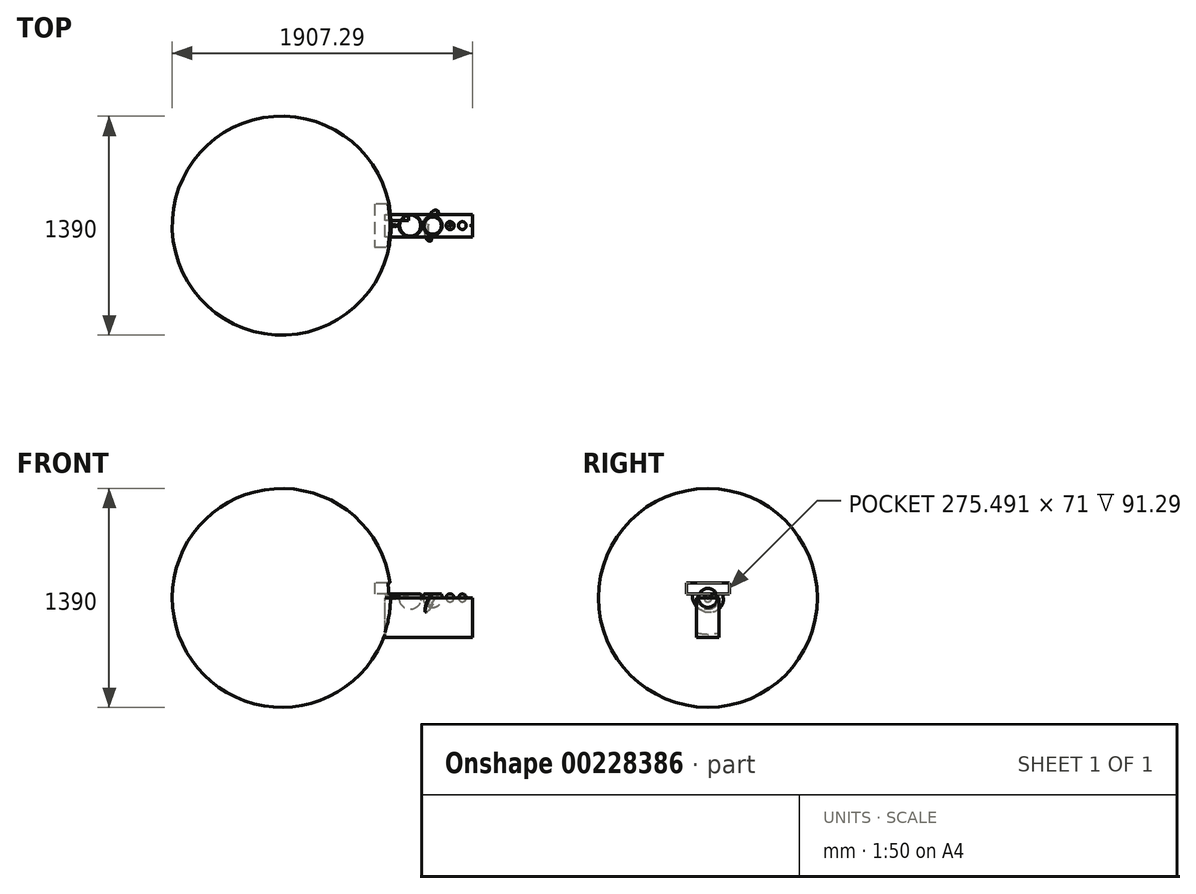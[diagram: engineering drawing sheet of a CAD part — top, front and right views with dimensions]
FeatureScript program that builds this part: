
annotation { "Feature Type Name" : "Feature", "Feature Type Description" : "" }
export const myFeature = defineFeature(function(context is Context, id is Id, definition is map)
    precondition{}
    {
        {
            assignVariable(context, id + "F0", {"name" : "SunD", "anyValue" : 1390});
        }
        {
            assignVariable(context, id + "F1", {"name" : "MercuryD", "anyValue" : 4.88});
        }
        {
            assignVariable(context, id + "F2", {"name" : "VenusD", "anyValue" : 12.1});
        }
        {
            assignVariable(context, id + "F3", {"name" : "EarthD", "anyValue" : 12.76});
        }
        {
            assignVariable(context, id + "F4", {"name" : "MarsD", "anyValue" : 6.8});
        }
        {
            assignVariable(context, id + "F5", {"name" : "JupiterD", "anyValue" : 143});
        }
        {
            assignVariable(context, id + "F6", {"name" : "SaturnD", "anyValue" : 120.5});
        }
        {
            assignVariable(context, id + "F7", {"name" : "UranusD", "anyValue" : 51.1});
        }
        {
            assignVariable(context, id + "F8", {"name" : "NeptuneD", "anyValue" : 49.5});
        }
        {
            assignVariable(context, id + "F9", {"name" : "PlutoD", "anyValue" : 2.35});
        }
        {
            var Q0;
            Q0=qCreatedBy(makeId("Top.planeOp"),FACE);
            var sketch = newSketch(context, id + "F10", { "sketchPlane" : qUnion([Q0])});
            skCircle(sketch, "E0", {"center": v(0, 0) * mm, "radius": 695 * mm});
            skCircle(sketch, "E1", {"center": v(0, 0) * mm, "radius": 2.44 * mm});
            skCircle(sketch, "E2", {"center": v(0, 0) * mm, "radius": 6.05 * mm});
            skCircle(sketch, "E3", {"center": v(0, 0) * mm, "radius": 6.38 * mm});
            skCircle(sketch, "E4", {"center": v(0, 0) * mm, "radius": 3.4 * mm});
            skCircle(sketch, "E5", {"center": v(0, 0) * mm, "radius": 71.5 * mm});
            skCircle(sketch, "E6", {"center": v(0, 0) * mm, "radius": 60.25 * mm});
            skCircle(sketch, "E7", {"center": v(0, 0) * mm, "radius": 25.55 * mm});
            skCircle(sketch, "E8", {"center": v(0, 0) * mm, "radius": 24.75 * mm});
            skCircle(sketch, "E9", {"center": v(0, 0) * mm, "radius": 1.18 * mm});
            skLineSegment(sketch, "E10", {"start": v(-694.4, -28.81) * mm, "end": v(0, 0) * mm});
            skLineSegment(sketch, "E11", {"start": v(0, 0) * mm, "end": v(694.4, 28.81) * mm});
            skCircle(sketch, "E12", {"center": v(0, 0) * mm, "radius": 100.25 * mm});
            skLineSegment(sketch, "E13", {"start": v(0, 0) * mm, "end": v(-4.16, 100.16) * mm, "construction": true});
            skSolve(sketch);
        }
        {
            var Q0;
            {var subQ0=sQuery(id+"F10.wireOp",EDGE,"E10");var subQ1=sQuery(id+"F10.wireOp",EDGE,"E1");var subQ2=makeQuery(id+"F10.imprint","INTERSECT",VERTEX,{"derivedFrom":[subQ1,subQ0]});Q0=makeQuery(id+"F10.imprint","IMPRINT",FACE,{"disambiguationData":[TD([[makeQuery(id+"F10.imprint","IMPRINT",EDGE,{"disambiguationData":[TD([[subQ2,1.0]])],"derivedFrom":subQ1}),1.0]])]});}
            var Q1;
            {var subQ0=sQuery(id+"F10.wireOp",EDGE,"E10");var subQ1=sQuery(id+"F10.wireOp",EDGE,"E9");var subQ2=makeQuery(id+"F10.imprint","INTERSECT",VERTEX,{"derivedFrom":[subQ1,subQ0]});Q1=makeQuery(id+"F10.imprint","IMPRINT",FACE,{"disambiguationData":[TD([[makeQuery(id+"F10.imprint","IMPRINT",EDGE,{"disambiguationData":[TD([[subQ2,1.0]])],"derivedFrom":subQ1}),1.0]])]});}
            var Q2;
            Q2=sQuery(id+"F10.wireOp",EDGE,"E10");
            revolve(context, id + "F11", {"entities" : qUnion([Q0, Q1]), "axis" : qUnion([Q2]), "revolveType" : RevolveType.FULL});
        }
        {
            var Q0;
            Q0=makeQuery(id+"F11.opRevolve","SWEPT_BODY",BODY,{"disambiguationData":[OSD([sQuery(id+"F10.wireOp",EDGE,"E1"),sQuery(id+"F10.wireOp",EDGE,"E10"),sQuery(id+"F10.wireOp",EDGE,"E11")])]});
            transform(context, id + "F12", {"entities" : qUnion([Q0]), "transformType" : TransformType.TRANSLATION_3D, "dx" : (getVariable(context, 'SunD') / 2 + getVariable(context, 'MercuryD') / 2 + 1) * mm, "dy" : 0 * mm, "dz" : 0 * mm, "makeCopy" : false});
        }
        {
            var Q0;
            {var subQ0=sQuery(id+"F10.wireOp",EDGE,"E10");var subQ1=sQuery(id+"F10.wireOp",EDGE,"E2");var subQ2=makeQuery(id+"F10.imprint","INTERSECT",VERTEX,{"derivedFrom":[subQ1,subQ0]});Q0=makeQuery(id+"F10.imprint","IMPRINT",FACE,{"disambiguationData":[TD([[makeQuery(id+"F10.imprint","IMPRINT",EDGE,{"disambiguationData":[TD([[subQ2,1.0]])],"derivedFrom":subQ1}),1.0]])]});}
            var Q1;
            {var subQ0=sQuery(id+"F10.wireOp",EDGE,"E10");var subQ1=sQuery(id+"F10.wireOp",EDGE,"E1");var subQ2=makeQuery(id+"F10.imprint","INTERSECT",VERTEX,{"derivedFrom":[subQ1,subQ0]});Q1=makeQuery(id+"F10.imprint","IMPRINT",FACE,{"disambiguationData":[TD([[makeQuery(id+"F10.imprint","IMPRINT",EDGE,{"disambiguationData":[TD([[subQ2,1.0]])],"derivedFrom":subQ1}),-1.0]])]});}
            var Q2;
            {var subQ0=sQuery(id+"F10.wireOp",EDGE,"E10");var subQ1=sQuery(id+"F10.wireOp",EDGE,"E1");var subQ2=makeQuery(id+"F10.imprint","INTERSECT",VERTEX,{"derivedFrom":[subQ1,subQ0]});Q2=makeQuery(id+"F10.imprint","IMPRINT",FACE,{"disambiguationData":[TD([[makeQuery(id+"F10.imprint","IMPRINT",EDGE,{"disambiguationData":[TD([[subQ2,1.0]])],"derivedFrom":subQ1}),1.0]])]});}
            var Q3;
            {var subQ0=sQuery(id+"F10.wireOp",EDGE,"E10");var subQ1=sQuery(id+"F10.wireOp",EDGE,"E9");var subQ2=makeQuery(id+"F10.imprint","INTERSECT",VERTEX,{"derivedFrom":[subQ1,subQ0]});Q3=makeQuery(id+"F10.imprint","IMPRINT",FACE,{"disambiguationData":[TD([[makeQuery(id+"F10.imprint","IMPRINT",EDGE,{"disambiguationData":[TD([[subQ2,1.0]])],"derivedFrom":subQ1}),1.0]])]});}
            var Q4;
            Q4=sQuery(id+"F10.wireOp",EDGE,"E11");
            revolve(context, id + "F13", {"entities" : qUnion([Q0, Q1, Q2, Q3]), "axis" : qUnion([Q4]), "revolveType" : RevolveType.FULL});
        }
        {
            var Q0;
            Q0=makeQuery(id+"F13.opRevolve","SWEPT_BODY",BODY,{"disambiguationData":[OSD([sQuery(id+"F10.wireOp",EDGE,"E2"),sQuery(id+"F10.wireOp",EDGE,"E10"),sQuery(id+"F10.wireOp",EDGE,"E11")])]});
            transform(context, id + "F14", {"entities" : qUnion([Q0]), "transformType" : TransformType.TRANSLATION_3D, "dx" : (getVariable(context, 'SunD') / 2 + getVariable(context, 'MercuryD') + getVariable(context, 'VenusD') / 2 + 0.72 / 0.39) * mm, "dy" : 0 * mm, "dz" : 0 * mm, "makeCopy" : false});
        }
        {
            var Q0;
            {var subQ0=sQuery(id+"F10.wireOp",EDGE,"E10");var subQ1=sQuery(id+"F10.wireOp",EDGE,"E2");var subQ2=makeQuery(id+"F10.imprint","INTERSECT",VERTEX,{"derivedFrom":[subQ1,subQ0]});Q0=makeQuery(id+"F10.imprint","IMPRINT",FACE,{"disambiguationData":[TD([[makeQuery(id+"F10.imprint","IMPRINT",EDGE,{"disambiguationData":[TD([[subQ2,1.0]])],"derivedFrom":subQ1}),-1.0]])]});}
            var Q1;
            {var subQ0=sQuery(id+"F10.wireOp",EDGE,"E10");var subQ1=sQuery(id+"F10.wireOp",EDGE,"E2");var subQ2=makeQuery(id+"F10.imprint","INTERSECT",VERTEX,{"derivedFrom":[subQ1,subQ0]});Q1=makeQuery(id+"F10.imprint","IMPRINT",FACE,{"disambiguationData":[TD([[makeQuery(id+"F10.imprint","IMPRINT",EDGE,{"disambiguationData":[TD([[subQ2,1.0]])],"derivedFrom":subQ1}),1.0]])]});}
            var Q2;
            {var subQ0=sQuery(id+"F10.wireOp",EDGE,"E10");var subQ1=sQuery(id+"F10.wireOp",EDGE,"E1");var subQ2=makeQuery(id+"F10.imprint","INTERSECT",VERTEX,{"derivedFrom":[subQ1,subQ0]});Q2=makeQuery(id+"F10.imprint","IMPRINT",FACE,{"disambiguationData":[TD([[makeQuery(id+"F10.imprint","IMPRINT",EDGE,{"disambiguationData":[TD([[subQ2,1.0]])],"derivedFrom":subQ1}),-1.0]])]});}
            var Q3;
            {var subQ0=sQuery(id+"F10.wireOp",EDGE,"E10");var subQ1=sQuery(id+"F10.wireOp",EDGE,"E1");var subQ2=makeQuery(id+"F10.imprint","INTERSECT",VERTEX,{"derivedFrom":[subQ1,subQ0]});Q3=makeQuery(id+"F10.imprint","IMPRINT",FACE,{"disambiguationData":[TD([[makeQuery(id+"F10.imprint","IMPRINT",EDGE,{"disambiguationData":[TD([[subQ2,1.0]])],"derivedFrom":subQ1}),1.0]])]});}
            var Q4;
            {var subQ0=sQuery(id+"F10.wireOp",EDGE,"E10");var subQ1=sQuery(id+"F10.wireOp",EDGE,"E9");var subQ2=makeQuery(id+"F10.imprint","INTERSECT",VERTEX,{"derivedFrom":[subQ1,subQ0]});Q4=makeQuery(id+"F10.imprint","IMPRINT",FACE,{"disambiguationData":[TD([[makeQuery(id+"F10.imprint","IMPRINT",EDGE,{"disambiguationData":[TD([[subQ2,1.0]])],"derivedFrom":subQ1}),1.0]])]});}
            var Q5;
            Q5=sQuery(id+"F10.wireOp",EDGE,"E10");
            revolve(context, id + "F15", {"entities" : qUnion([Q0, Q1, Q2, Q3, Q4]), "axis" : qUnion([Q5]), "revolveType" : RevolveType.FULL});
        }
        {
            var Q0;
            Q0=makeQuery(id+"F15.opRevolve","SWEPT_BODY",BODY,{"disambiguationData":[OSD([sQuery(id+"F10.wireOp",EDGE,"E3"),sQuery(id+"F10.wireOp",EDGE,"E10"),sQuery(id+"F10.wireOp",EDGE,"E11")])]});
            transform(context, id + "F16", {"entities" : qUnion([Q0]), "transformType" : TransformType.TRANSLATION_3D, "dx" : (getVariable(context, 'SunD') / 2 + getVariable(context, 'MercuryD') + getVariable(context, 'VenusD') + getVariable(context, 'EarthD') / 2 + 1 / 0.39) * mm, "dy" : 0 * mm, "dz" : 0 * mm, "makeCopy" : false});
        }
        {
            var Q0;
            {var subQ0=sQuery(id+"F10.wireOp",EDGE,"E10");var subQ1=sQuery(id+"F10.wireOp",EDGE,"E1");var subQ2=makeQuery(id+"F10.imprint","INTERSECT",VERTEX,{"derivedFrom":[subQ1,subQ0]});Q0=makeQuery(id+"F10.imprint","IMPRINT",FACE,{"disambiguationData":[TD([[makeQuery(id+"F10.imprint","IMPRINT",EDGE,{"disambiguationData":[TD([[subQ2,1.0]])],"derivedFrom":subQ1}),-1.0]])]});}
            var Q1;
            {var subQ0=sQuery(id+"F10.wireOp",EDGE,"E10");var subQ1=sQuery(id+"F10.wireOp",EDGE,"E1");var subQ2=makeQuery(id+"F10.imprint","INTERSECT",VERTEX,{"derivedFrom":[subQ1,subQ0]});Q1=makeQuery(id+"F10.imprint","IMPRINT",FACE,{"disambiguationData":[TD([[makeQuery(id+"F10.imprint","IMPRINT",EDGE,{"disambiguationData":[TD([[subQ2,1.0]])],"derivedFrom":subQ1}),1.0]])]});}
            var Q2;
            {var subQ0=sQuery(id+"F10.wireOp",EDGE,"E10");var subQ1=sQuery(id+"F10.wireOp",EDGE,"E9");var subQ2=makeQuery(id+"F10.imprint","INTERSECT",VERTEX,{"derivedFrom":[subQ1,subQ0]});Q2=makeQuery(id+"F10.imprint","IMPRINT",FACE,{"disambiguationData":[TD([[makeQuery(id+"F10.imprint","IMPRINT",EDGE,{"disambiguationData":[TD([[subQ2,1.0]])],"derivedFrom":subQ1}),1.0]])]});}
            var Q3;
            Q3=sQuery(id+"F10.wireOp",EDGE,"E11");
            revolve(context, id + "F17", {"entities" : qUnion([Q0, Q1, Q2]), "axis" : qUnion([Q3]), "revolveType" : RevolveType.FULL});
        }
        {
            var Q0;
            Q0=makeQuery(id+"F17.opRevolve","SWEPT_BODY",BODY,{"disambiguationData":[OSD([sQuery(id+"F10.wireOp",EDGE,"E4"),sQuery(id+"F10.wireOp",EDGE,"E10"),sQuery(id+"F10.wireOp",EDGE,"E11")])]});
            transform(context, id + "F18", {"entities" : qUnion([Q0]), "transformType" : TransformType.TRANSLATION_3D, "dx" : (getVariable(context, 'SunD') / 2 + getVariable(context, 'MercuryD') + getVariable(context, 'VenusD') + getVariable(context, 'EarthD') + getVariable(context, 'MarsD') / 2 + 1.52 / 0.39) * mm, "dy" : 0 * mm, "dz" : 0 * mm, "makeCopy" : false});
        }
        {
            var Q0;
            {var subQ0=sQuery(id+"F10.wireOp",EDGE,"E10");var subQ1=sQuery(id+"F10.wireOp",EDGE,"E5");var subQ2=makeQuery(id+"F10.imprint","INTERSECT",VERTEX,{"derivedFrom":[subQ1,subQ0]});Q0=makeQuery(id+"F10.imprint","IMPRINT",FACE,{"disambiguationData":[TD([[makeQuery(id+"F10.imprint","IMPRINT",EDGE,{"disambiguationData":[TD([[subQ2,1.0]])],"derivedFrom":subQ1}),1.0]])]});}
            var Q1;
            {var subQ0=sQuery(id+"F10.wireOp",EDGE,"E10");var subQ1=sQuery(id+"F10.wireOp",EDGE,"E6");var subQ2=makeQuery(id+"F10.imprint","INTERSECT",VERTEX,{"derivedFrom":[subQ1,subQ0]});Q1=makeQuery(id+"F10.imprint","IMPRINT",FACE,{"disambiguationData":[TD([[makeQuery(id+"F10.imprint","IMPRINT",EDGE,{"disambiguationData":[TD([[subQ2,1.0]])],"derivedFrom":subQ1}),1.0]])]});}
            var Q2;
            {var subQ0=sQuery(id+"F10.wireOp",EDGE,"E10");var subQ1=sQuery(id+"F10.wireOp",EDGE,"E3");var subQ2=makeQuery(id+"F10.imprint","INTERSECT",VERTEX,{"derivedFrom":[subQ1,subQ0]});Q2=makeQuery(id+"F10.imprint","IMPRINT",FACE,{"disambiguationData":[TD([[makeQuery(id+"F10.imprint","IMPRINT",EDGE,{"disambiguationData":[TD([[subQ2,1.0]])],"derivedFrom":subQ1}),-1.0]])]});}
            var Q3;
            {var subQ0=sQuery(id+"F10.wireOp",EDGE,"E10");var subQ1=sQuery(id+"F10.wireOp",EDGE,"E7");var subQ2=makeQuery(id+"F10.imprint","INTERSECT",VERTEX,{"derivedFrom":[subQ1,subQ0]});Q3=makeQuery(id+"F10.imprint","IMPRINT",FACE,{"disambiguationData":[TD([[makeQuery(id+"F10.imprint","IMPRINT",EDGE,{"disambiguationData":[TD([[subQ2,1.0]])],"derivedFrom":subQ1}),1.0]])]});}
            var Q4;
            {var subQ0=sQuery(id+"F10.wireOp",EDGE,"E10");var subQ1=sQuery(id+"F10.wireOp",EDGE,"E2");var subQ2=makeQuery(id+"F10.imprint","INTERSECT",VERTEX,{"derivedFrom":[subQ1,subQ0]});Q4=makeQuery(id+"F10.imprint","IMPRINT",FACE,{"disambiguationData":[TD([[makeQuery(id+"F10.imprint","IMPRINT",EDGE,{"disambiguationData":[TD([[subQ2,1.0]])],"derivedFrom":subQ1}),1.0]])]});}
            var Q5;
            {var subQ0=sQuery(id+"F10.wireOp",EDGE,"E10");var subQ1=sQuery(id+"F10.wireOp",EDGE,"E1");var subQ2=makeQuery(id+"F10.imprint","INTERSECT",VERTEX,{"derivedFrom":[subQ1,subQ0]});Q5=makeQuery(id+"F10.imprint","IMPRINT",FACE,{"disambiguationData":[TD([[makeQuery(id+"F10.imprint","IMPRINT",EDGE,{"disambiguationData":[TD([[subQ2,1.0]])],"derivedFrom":subQ1}),-1.0]])]});}
            var Q6;
            {var subQ0=sQuery(id+"F10.wireOp",EDGE,"E10");var subQ1=sQuery(id+"F10.wireOp",EDGE,"E1");var subQ2=makeQuery(id+"F10.imprint","INTERSECT",VERTEX,{"derivedFrom":[subQ1,subQ0]});Q6=makeQuery(id+"F10.imprint","IMPRINT",FACE,{"disambiguationData":[TD([[makeQuery(id+"F10.imprint","IMPRINT",EDGE,{"disambiguationData":[TD([[subQ2,1.0]])],"derivedFrom":subQ1}),1.0]])]});}
            var Q7;
            {var subQ0=sQuery(id+"F10.wireOp",EDGE,"E10");var subQ1=sQuery(id+"F10.wireOp",EDGE,"E9");var subQ2=makeQuery(id+"F10.imprint","INTERSECT",VERTEX,{"derivedFrom":[subQ1,subQ0]});Q7=makeQuery(id+"F10.imprint","IMPRINT",FACE,{"disambiguationData":[TD([[makeQuery(id+"F10.imprint","IMPRINT",EDGE,{"disambiguationData":[TD([[subQ2,1.0]])],"derivedFrom":subQ1}),1.0]])]});}
            var Q8;
            {var subQ0=sQuery(id+"F10.wireOp",EDGE,"E10");var subQ1=sQuery(id+"F10.wireOp",EDGE,"E2");var subQ2=makeQuery(id+"F10.imprint","INTERSECT",VERTEX,{"derivedFrom":[subQ1,subQ0]});Q8=makeQuery(id+"F10.imprint","IMPRINT",FACE,{"disambiguationData":[TD([[makeQuery(id+"F10.imprint","IMPRINT",EDGE,{"disambiguationData":[TD([[subQ2,1.0]])],"derivedFrom":subQ1}),-1.0]])]});}
            var Q9;
            Q9=sQuery(id+"F10.wireOp",EDGE,"E11");
            revolve(context, id + "F19", {"entities" : qUnion([Q0, Q1, Q2, Q3, Q4, Q5, Q6, Q7, Q8]), "axis" : qUnion([Q9]), "revolveType" : RevolveType.FULL});
        }
        {
            var Q0;
            Q0=makeQuery(id+"F19.opRevolve","SWEPT_BODY",BODY,{"disambiguationData":[OSD([sQuery(id+"F10.wireOp",EDGE,"E5"),sQuery(id+"F10.wireOp",EDGE,"E10"),sQuery(id+"F10.wireOp",EDGE,"E11")])]});
            transform(context, id + "F20", {"entities" : qUnion([Q0]), "transformType" : TransformType.TRANSLATION_3D, "dx" : (getVariable(context, 'SunD') / 2 + getVariable(context, 'MercuryD') + getVariable(context, 'VenusD') + getVariable(context, 'EarthD') + getVariable(context, 'MarsD') + getVariable(context, 'JupiterD') / 2 + 5.3 / 0.39) * mm, "dy" : 0 * mm, "dz" : 0 * mm, "makeCopy" : false});
        }
        {
            var Q0;
            {var subQ0=sQuery(id+"F10.wireOp",EDGE,"E10");var subQ1=sQuery(id+"F10.wireOp",EDGE,"E6");var subQ2=makeQuery(id+"F10.imprint","INTERSECT",VERTEX,{"derivedFrom":[subQ1,subQ0]});Q0=makeQuery(id+"F10.imprint","IMPRINT",FACE,{"disambiguationData":[TD([[makeQuery(id+"F10.imprint","IMPRINT",EDGE,{"disambiguationData":[TD([[subQ2,1.0]])],"derivedFrom":subQ1}),1.0]])]});}
            var Q1;
            {var subQ0=sQuery(id+"F10.wireOp",EDGE,"E10");var subQ1=sQuery(id+"F10.wireOp",EDGE,"E7");var subQ2=makeQuery(id+"F10.imprint","INTERSECT",VERTEX,{"derivedFrom":[subQ1,subQ0]});Q1=makeQuery(id+"F10.imprint","IMPRINT",FACE,{"disambiguationData":[TD([[makeQuery(id+"F10.imprint","IMPRINT",EDGE,{"disambiguationData":[TD([[subQ2,1.0]])],"derivedFrom":subQ1}),1.0]])]});}
            var Q2;
            {var subQ0=sQuery(id+"F10.wireOp",EDGE,"E10");var subQ1=sQuery(id+"F10.wireOp",EDGE,"E3");var subQ2=makeQuery(id+"F10.imprint","INTERSECT",VERTEX,{"derivedFrom":[subQ1,subQ0]});Q2=makeQuery(id+"F10.imprint","IMPRINT",FACE,{"disambiguationData":[TD([[makeQuery(id+"F10.imprint","IMPRINT",EDGE,{"disambiguationData":[TD([[subQ2,1.0]])],"derivedFrom":subQ1}),-1.0]])]});}
            var Q3;
            {var subQ0=sQuery(id+"F10.wireOp",EDGE,"E10");var subQ1=sQuery(id+"F10.wireOp",EDGE,"E2");var subQ2=makeQuery(id+"F10.imprint","INTERSECT",VERTEX,{"derivedFrom":[subQ1,subQ0]});Q3=makeQuery(id+"F10.imprint","IMPRINT",FACE,{"disambiguationData":[TD([[makeQuery(id+"F10.imprint","IMPRINT",EDGE,{"disambiguationData":[TD([[subQ2,1.0]])],"derivedFrom":subQ1}),1.0]])]});}
            var Q4;
            {var subQ0=sQuery(id+"F10.wireOp",EDGE,"E10");var subQ1=sQuery(id+"F10.wireOp",EDGE,"E1");var subQ2=makeQuery(id+"F10.imprint","INTERSECT",VERTEX,{"derivedFrom":[subQ1,subQ0]});Q4=makeQuery(id+"F10.imprint","IMPRINT",FACE,{"disambiguationData":[TD([[makeQuery(id+"F10.imprint","IMPRINT",EDGE,{"disambiguationData":[TD([[subQ2,1.0]])],"derivedFrom":subQ1}),-1.0]])]});}
            var Q5;
            {var subQ0=sQuery(id+"F10.wireOp",EDGE,"E10");var subQ1=sQuery(id+"F10.wireOp",EDGE,"E1");var subQ2=makeQuery(id+"F10.imprint","INTERSECT",VERTEX,{"derivedFrom":[subQ1,subQ0]});Q5=makeQuery(id+"F10.imprint","IMPRINT",FACE,{"disambiguationData":[TD([[makeQuery(id+"F10.imprint","IMPRINT",EDGE,{"disambiguationData":[TD([[subQ2,1.0]])],"derivedFrom":subQ1}),1.0]])]});}
            var Q6;
            {var subQ0=sQuery(id+"F10.wireOp",EDGE,"E10");var subQ1=sQuery(id+"F10.wireOp",EDGE,"E9");var subQ2=makeQuery(id+"F10.imprint","INTERSECT",VERTEX,{"derivedFrom":[subQ1,subQ0]});Q6=makeQuery(id+"F10.imprint","IMPRINT",FACE,{"disambiguationData":[TD([[makeQuery(id+"F10.imprint","IMPRINT",EDGE,{"disambiguationData":[TD([[subQ2,1.0]])],"derivedFrom":subQ1}),1.0]])]});}
            var Q7;
            {var subQ0=sQuery(id+"F10.wireOp",EDGE,"E10");var subQ1=sQuery(id+"F10.wireOp",EDGE,"E2");var subQ2=makeQuery(id+"F10.imprint","INTERSECT",VERTEX,{"derivedFrom":[subQ1,subQ0]});Q7=makeQuery(id+"F10.imprint","IMPRINT",FACE,{"disambiguationData":[TD([[makeQuery(id+"F10.imprint","IMPRINT",EDGE,{"disambiguationData":[TD([[subQ2,1.0]])],"derivedFrom":subQ1}),-1.0]])]});}
            var Q8;
            Q8=sQuery(id+"F10.wireOp",EDGE,"E10");
            revolve(context, id + "F21", {"entities" : qUnion([Q0, Q1, Q2, Q3, Q4, Q5, Q6, Q7]), "axis" : qUnion([Q8]), "revolveType" : RevolveType.FULL});
        }
        {
            var Q0;
            {var subQ0=sQuery(id+"F10.wireOp",EDGE,"E10");var subQ1=sQuery(id+"F10.wireOp",EDGE,"E5");var subQ2=makeQuery(id+"F10.imprint","INTERSECT",VERTEX,{"derivedFrom":[subQ1,subQ0]});Q0=makeQuery(id+"F10.imprint","IMPRINT",FACE,{"disambiguationData":[TD([[makeQuery(id+"F10.imprint","IMPRINT",EDGE,{"disambiguationData":[TD([[subQ2,1.0]])],"derivedFrom":subQ1}),-1.0]])]});}
            var Q1;
            {var subQ0=sQuery(id+"F10.wireOp",EDGE,"E10");var subQ1=sQuery(id+"F10.wireOp",EDGE,"E5");var subQ2=makeQuery(id+"F10.imprint","INTERSECT",VERTEX,{"derivedFrom":[subQ1,subQ0]});Q1=makeQuery(id+"F10.imprint","IMPRINT",FACE,{"disambiguationData":[TD([[makeQuery(id+"F10.imprint","IMPRINT",EDGE,{"disambiguationData":[TD([[subQ2,1.0]])],"derivedFrom":subQ1}),1.0]])]});}
            var Q2;
            {var subQ0=sQuery(id+"F10.wireOp",EDGE,"E10");var subQ1=sQuery(id+"F10.wireOp",EDGE,"E5");var subQ2=makeQuery(id+"F10.imprint","INTERSECT",VERTEX,{"derivedFrom":[subQ1,subQ0]});Q2=makeQuery(id+"F10.imprint","IMPRINT",FACE,{"disambiguationData":[TD([[makeQuery(id+"F10.imprint","IMPRINT",EDGE,{"disambiguationData":[TD([[subQ2,-1.0]])],"derivedFrom":subQ1}),1.0]])]});}
            var Q3;
            {var subQ0=sQuery(id+"F10.wireOp",EDGE,"E10");var subQ1=sQuery(id+"F10.wireOp",EDGE,"E5");var subQ2=makeQuery(id+"F10.imprint","INTERSECT",VERTEX,{"derivedFrom":[subQ1,subQ0]});Q3=makeQuery(id+"F10.imprint","IMPRINT",FACE,{"disambiguationData":[TD([[makeQuery(id+"F10.imprint","IMPRINT",EDGE,{"disambiguationData":[TD([[subQ2,-1.0]])],"derivedFrom":subQ1}),-1.0]])]});}
            var Q4;
            {var subQ0=sQuery(id+"F10.wireOp",EDGE,"E10");var subQ1=sQuery(id+"F10.wireOp",EDGE,"E6");var subQ2=makeQuery(id+"F10.imprint","INTERSECT",VERTEX,{"derivedFrom":[subQ1,subQ0]});Q4=makeQuery(id+"F10.imprint","IMPRINT",FACE,{"disambiguationData":[TD([[makeQuery(id+"F10.imprint","IMPRINT",EDGE,{"disambiguationData":[TD([[subQ2,-1.0]])],"derivedFrom":subQ1}),1.0]])]});}
            var Q5;
            {var subQ0=sQuery(id+"F10.wireOp",EDGE,"E10");var subQ1=sQuery(id+"F10.wireOp",EDGE,"E6");var subQ2=makeQuery(id+"F10.imprint","INTERSECT",VERTEX,{"derivedFrom":[subQ1,subQ0]});Q5=makeQuery(id+"F10.imprint","IMPRINT",FACE,{"disambiguationData":[TD([[makeQuery(id+"F10.imprint","IMPRINT",EDGE,{"disambiguationData":[TD([[subQ2,1.0]])],"derivedFrom":subQ1}),1.0]])]});}
            extrude(context, id + "F22", {"entities" : qUnion([Q0, Q1, Q2, Q3, Q4, Q5]), "operationType" : NewBodyOperationType.ADD, "depth" : 3 * mm, "symmetric" : true});
        }
        {
            var Q0;
            Q0=makeQuery(id+"F21.opRevolve","SWEPT_BODY",BODY,{"disambiguationData":[OSD([sQuery(id+"F10.wireOp",EDGE,"E6"),sQuery(id+"F10.wireOp",EDGE,"E10"),sQuery(id+"F10.wireOp",EDGE,"E11")])]});
            var Q1;
            Q1=sQuery(id+"F10.wireOp",EDGE,"E13");
            transform(context, id + "F23", {"entities" : qUnion([Q0]), "transformType" : TransformType.ROTATION, "transformAxis" : qUnion([Q1]), "angle" : 120 * degree, "makeCopy" : false});
        }
        {
            var Q0;
            Q0=makeQuery(id+"F21.opRevolve","SWEPT_BODY",BODY,{"disambiguationData":[OSD([sQuery(id+"F10.wireOp",EDGE,"E6"),sQuery(id+"F10.wireOp",EDGE,"E10"),sQuery(id+"F10.wireOp",EDGE,"E11")])]});
            var Q1;
            Q1=sQuery(id+"F10.wireOp",EDGE,"E10");
            transform(context, id + "F24", {"entities" : qUnion([Q0]), "transformType" : TransformType.ROTATION, "transformAxis" : qUnion([Q1]), "angle" : 30 * degree, "oppositeDirection" : true, "makeCopy" : false});
        }
        {
            var Q0;
            Q0=makeQuery(id+"F21.opRevolve","SWEPT_BODY",BODY,{"disambiguationData":[OSD([sQuery(id+"F10.wireOp",EDGE,"E6"),sQuery(id+"F10.wireOp",EDGE,"E10"),sQuery(id+"F10.wireOp",EDGE,"E11")])]});
            transform(context, id + "F25", {"entities" : qUnion([Q0]), "transformType" : TransformType.TRANSLATION_3D, "dx" : (getVariable(context, 'SunD') / 2 + getVariable(context, 'MercuryD') + getVariable(context, 'VenusD') + getVariable(context, 'EarthD') + getVariable(context, 'MarsD') + getVariable(context, 'JupiterD') + getVariable(context, 'SaturnD') / 2 + 9.52 / 0.39) * mm, "dy" : 0 * mm, "dz" : 0 * mm, "makeCopy" : false});
        }
        {
            var Q0;
            {var subQ0=sQuery(id+"F10.wireOp",EDGE,"E10");var subQ1=sQuery(id+"F10.wireOp",EDGE,"E3");var subQ2=makeQuery(id+"F10.imprint","INTERSECT",VERTEX,{"derivedFrom":[subQ1,subQ0]});Q0=makeQuery(id+"F10.imprint","IMPRINT",FACE,{"disambiguationData":[TD([[makeQuery(id+"F10.imprint","IMPRINT",EDGE,{"disambiguationData":[TD([[subQ2,1.0]])],"derivedFrom":subQ1}),-1.0]])]});}
            var Q1;
            {var subQ0=sQuery(id+"F10.wireOp",EDGE,"E10");var subQ1=sQuery(id+"F10.wireOp",EDGE,"E2");var subQ2=makeQuery(id+"F10.imprint","INTERSECT",VERTEX,{"derivedFrom":[subQ1,subQ0]});Q1=makeQuery(id+"F10.imprint","IMPRINT",FACE,{"disambiguationData":[TD([[makeQuery(id+"F10.imprint","IMPRINT",EDGE,{"disambiguationData":[TD([[subQ2,1.0]])],"derivedFrom":subQ1}),1.0]])]});}
            var Q2;
            {var subQ0=sQuery(id+"F10.wireOp",EDGE,"E10");var subQ1=sQuery(id+"F10.wireOp",EDGE,"E1");var subQ2=makeQuery(id+"F10.imprint","INTERSECT",VERTEX,{"derivedFrom":[subQ1,subQ0]});Q2=makeQuery(id+"F10.imprint","IMPRINT",FACE,{"disambiguationData":[TD([[makeQuery(id+"F10.imprint","IMPRINT",EDGE,{"disambiguationData":[TD([[subQ2,1.0]])],"derivedFrom":subQ1}),-1.0]])]});}
            var Q3;
            {var subQ0=sQuery(id+"F10.wireOp",EDGE,"E10");var subQ1=sQuery(id+"F10.wireOp",EDGE,"E1");var subQ2=makeQuery(id+"F10.imprint","INTERSECT",VERTEX,{"derivedFrom":[subQ1,subQ0]});Q3=makeQuery(id+"F10.imprint","IMPRINT",FACE,{"disambiguationData":[TD([[makeQuery(id+"F10.imprint","IMPRINT",EDGE,{"disambiguationData":[TD([[subQ2,1.0]])],"derivedFrom":subQ1}),1.0]])]});}
            var Q4;
            {var subQ0=sQuery(id+"F10.wireOp",EDGE,"E10");var subQ1=sQuery(id+"F10.wireOp",EDGE,"E9");var subQ2=makeQuery(id+"F10.imprint","INTERSECT",VERTEX,{"derivedFrom":[subQ1,subQ0]});Q4=makeQuery(id+"F10.imprint","IMPRINT",FACE,{"disambiguationData":[TD([[makeQuery(id+"F10.imprint","IMPRINT",EDGE,{"disambiguationData":[TD([[subQ2,1.0]])],"derivedFrom":subQ1}),1.0]])]});}
            var Q5;
            {var subQ0=sQuery(id+"F10.wireOp",EDGE,"E10");var subQ1=sQuery(id+"F10.wireOp",EDGE,"E2");var subQ2=makeQuery(id+"F10.imprint","INTERSECT",VERTEX,{"derivedFrom":[subQ1,subQ0]});Q5=makeQuery(id+"F10.imprint","IMPRINT",FACE,{"disambiguationData":[TD([[makeQuery(id+"F10.imprint","IMPRINT",EDGE,{"disambiguationData":[TD([[subQ2,1.0]])],"derivedFrom":subQ1}),-1.0]])]});}
            var Q6;
            {var subQ0=sQuery(id+"F10.wireOp",EDGE,"E10");var subQ1=sQuery(id+"F10.wireOp",EDGE,"E7");var subQ2=makeQuery(id+"F10.imprint","INTERSECT",VERTEX,{"derivedFrom":[subQ1,subQ0]});Q6=makeQuery(id+"F10.imprint","IMPRINT",FACE,{"disambiguationData":[TD([[makeQuery(id+"F10.imprint","IMPRINT",EDGE,{"disambiguationData":[TD([[subQ2,1.0]])],"derivedFrom":subQ1}),1.0]])]});}
            var Q7;
            Q7=sQuery(id+"F10.wireOp",EDGE,"E10");
            revolve(context, id + "F26", {"entities" : qUnion([Q0, Q1, Q2, Q3, Q4, Q5, Q6]), "axis" : qUnion([Q7]), "revolveType" : RevolveType.FULL});
        }
        {
            var Q0;
            Q0=makeQuery(id+"F26.opRevolve","SWEPT_BODY",BODY,{"disambiguationData":[OSD([sQuery(id+"F10.wireOp",EDGE,"E7"),sQuery(id+"F10.wireOp",EDGE,"E10"),sQuery(id+"F10.wireOp",EDGE,"E11")])]});
            transform(context, id + "F27", {"entities" : qUnion([Q0]), "transformType" : TransformType.TRANSLATION_3D, "dx" : (getVariable(context, 'SunD') / 2 + getVariable(context, 'MercuryD') + getVariable(context, 'VenusD') + getVariable(context, 'EarthD') + getVariable(context, 'MarsD') + getVariable(context, 'JupiterD') + getVariable(context, 'SaturnD') + getVariable(context, 'UranusD') / 2 + 19.2 / 0.39) * mm, "dy" : 0 * mm, "dz" : 0 * mm, "makeCopy" : false});
        }
        {
            var Q0;
            {var subQ0=sQuery(id+"F10.wireOp",EDGE,"E10");var subQ1=sQuery(id+"F10.wireOp",EDGE,"E9");var subQ2=makeQuery(id+"F10.imprint","INTERSECT",VERTEX,{"derivedFrom":[subQ1,subQ0]});Q0=makeQuery(id+"F10.imprint","IMPRINT",FACE,{"disambiguationData":[TD([[makeQuery(id+"F10.imprint","IMPRINT",EDGE,{"disambiguationData":[TD([[subQ2,1.0]])],"derivedFrom":subQ1}),1.0]])]});}
            var Q1;
            {var subQ0=sQuery(id+"F10.wireOp",EDGE,"E10");var subQ1=sQuery(id+"F10.wireOp",EDGE,"E1");var subQ2=makeQuery(id+"F10.imprint","INTERSECT",VERTEX,{"derivedFrom":[subQ1,subQ0]});Q1=makeQuery(id+"F10.imprint","IMPRINT",FACE,{"disambiguationData":[TD([[makeQuery(id+"F10.imprint","IMPRINT",EDGE,{"disambiguationData":[TD([[subQ2,1.0]])],"derivedFrom":subQ1}),1.0]])]});}
            var Q2;
            {var subQ0=sQuery(id+"F10.wireOp",EDGE,"E10");var subQ1=sQuery(id+"F10.wireOp",EDGE,"E1");var subQ2=makeQuery(id+"F10.imprint","INTERSECT",VERTEX,{"derivedFrom":[subQ1,subQ0]});Q2=makeQuery(id+"F10.imprint","IMPRINT",FACE,{"disambiguationData":[TD([[makeQuery(id+"F10.imprint","IMPRINT",EDGE,{"disambiguationData":[TD([[subQ2,1.0]])],"derivedFrom":subQ1}),-1.0]])]});}
            var Q3;
            {var subQ0=sQuery(id+"F10.wireOp",EDGE,"E10");var subQ1=sQuery(id+"F10.wireOp",EDGE,"E2");var subQ2=makeQuery(id+"F10.imprint","INTERSECT",VERTEX,{"derivedFrom":[subQ1,subQ0]});Q3=makeQuery(id+"F10.imprint","IMPRINT",FACE,{"disambiguationData":[TD([[makeQuery(id+"F10.imprint","IMPRINT",EDGE,{"disambiguationData":[TD([[subQ2,1.0]])],"derivedFrom":subQ1}),1.0]])]});}
            var Q4;
            {var subQ0=sQuery(id+"F10.wireOp",EDGE,"E10");var subQ1=sQuery(id+"F10.wireOp",EDGE,"E2");var subQ2=makeQuery(id+"F10.imprint","INTERSECT",VERTEX,{"derivedFrom":[subQ1,subQ0]});Q4=makeQuery(id+"F10.imprint","IMPRINT",FACE,{"disambiguationData":[TD([[makeQuery(id+"F10.imprint","IMPRINT",EDGE,{"disambiguationData":[TD([[subQ2,1.0]])],"derivedFrom":subQ1}),-1.0]])]});}
            var Q5;
            {var subQ0=sQuery(id+"F10.wireOp",EDGE,"E10");var subQ1=sQuery(id+"F10.wireOp",EDGE,"E3");var subQ2=makeQuery(id+"F10.imprint","INTERSECT",VERTEX,{"derivedFrom":[subQ1,subQ0]});Q5=makeQuery(id+"F10.imprint","IMPRINT",FACE,{"disambiguationData":[TD([[makeQuery(id+"F10.imprint","IMPRINT",EDGE,{"disambiguationData":[TD([[subQ2,1.0]])],"derivedFrom":subQ1}),-1.0]])]});}
            var Q6;
            Q6=sQuery(id+"F10.wireOp",EDGE,"E10");
            revolve(context, id + "F28", {"entities" : qUnion([Q0, Q1, Q2, Q3, Q4, Q5]), "axis" : qUnion([Q6]), "revolveType" : RevolveType.FULL});
        }
        {
            var Q0;
            Q0=makeQuery(id+"F28.opRevolve","SWEPT_BODY",BODY,{"disambiguationData":[OSD([sQuery(id+"F10.wireOp",EDGE,"E8"),sQuery(id+"F10.wireOp",EDGE,"E10"),sQuery(id+"F10.wireOp",EDGE,"E11")])]});
            transform(context, id + "F29", {"entities" : qUnion([Q0]), "transformType" : TransformType.TRANSLATION_3D, "dx" : (getVariable(context, 'SunD') / 2 + getVariable(context, 'MercuryD') + getVariable(context, 'VenusD') + getVariable(context, 'EarthD') + getVariable(context, 'MarsD') + getVariable(context, 'JupiterD') + getVariable(context, 'SaturnD') + getVariable(context, 'UranusD') + getVariable(context, 'NeptuneD') / 2 + 30 / 0.39) * mm, "dy" : 0 * mm, "dz" : 0 * mm, "makeCopy" : false});
        }
        {
            var Q0;
            {var subQ0=sQuery(id+"F10.wireOp",EDGE,"E10");var subQ1=sQuery(id+"F10.wireOp",EDGE,"E9");var subQ2=makeQuery(id+"F10.imprint","INTERSECT",VERTEX,{"derivedFrom":[subQ1,subQ0]});Q0=makeQuery(id+"F10.imprint","IMPRINT",FACE,{"disambiguationData":[TD([[makeQuery(id+"F10.imprint","IMPRINT",EDGE,{"disambiguationData":[TD([[subQ2,1.0]])],"derivedFrom":subQ1}),1.0]])]});}
            var Q1;
            Q1=sQuery(id+"F10.wireOp",EDGE,"E10");
            revolve(context, id + "F30", {"entities" : qUnion([Q0]), "axis" : qUnion([Q1]), "revolveType" : RevolveType.FULL});
        }
        {
            var Q0;
            Q0=makeQuery(id+"F30.opRevolve","SWEPT_BODY",BODY,{"disambiguationData":[OSD([sQuery(id+"F10.wireOp",EDGE,"E9"),sQuery(id+"F10.wireOp",EDGE,"E10"),sQuery(id+"F10.wireOp",EDGE,"E11")])]});
            transform(context, id + "F31", {"entities" : qUnion([Q0]), "transformType" : TransformType.TRANSLATION_3D, "dx" : (getVariable(context, 'SunD') / 2 + getVariable(context, 'MercuryD') + getVariable(context, 'VenusD') + getVariable(context, 'EarthD') + getVariable(context, 'MarsD') + getVariable(context, 'JupiterD') + getVariable(context, 'SaturnD') + getVariable(context, 'UranusD') + getVariable(context, 'NeptuneD') + getVariable(context, 'PlutoD') / 2 + 39.5 / 0.39) * mm, "dy" : 0 * mm, "dz" : 0 * mm, "makeCopy" : false});
        }
        {
            var Q0;
            {var subQ0=sQuery(id+"F10.wireOp",EDGE,"E10");var subQ1=sQuery(id+"F10.wireOp",EDGE,"E0");var subQ2=makeQuery(id+"F10.imprint","INTERSECT",VERTEX,{"derivedFrom":[subQ1,subQ0]});Q0=makeQuery(id+"F10.imprint","IMPRINT",FACE,{"disambiguationData":[TD([[makeQuery(id+"F10.imprint","IMPRINT",EDGE,{"disambiguationData":[TD([[subQ2,1.0]])],"derivedFrom":subQ1}),1.0]])]});}
            var Q1;
            {var subQ0=sQuery(id+"F10.wireOp",EDGE,"E10");var subQ1=sQuery(id+"F10.wireOp",EDGE,"E5");var subQ2=makeQuery(id+"F10.imprint","INTERSECT",VERTEX,{"derivedFrom":[subQ1,subQ0]});Q1=makeQuery(id+"F10.imprint","IMPRINT",FACE,{"disambiguationData":[TD([[makeQuery(id+"F10.imprint","IMPRINT",EDGE,{"disambiguationData":[TD([[subQ2,1.0]])],"derivedFrom":subQ1}),-1.0]])]});}
            var Q2;
            {var subQ0=sQuery(id+"F10.wireOp",EDGE,"E10");var subQ1=sQuery(id+"F10.wireOp",EDGE,"E5");var subQ2=makeQuery(id+"F10.imprint","INTERSECT",VERTEX,{"derivedFrom":[subQ1,subQ0]});Q2=makeQuery(id+"F10.imprint","IMPRINT",FACE,{"disambiguationData":[TD([[makeQuery(id+"F10.imprint","IMPRINT",EDGE,{"disambiguationData":[TD([[subQ2,1.0]])],"derivedFrom":subQ1}),1.0]])]});}
            var Q3;
            {var subQ0=sQuery(id+"F10.wireOp",EDGE,"E10");var subQ1=sQuery(id+"F10.wireOp",EDGE,"E6");var subQ2=makeQuery(id+"F10.imprint","INTERSECT",VERTEX,{"derivedFrom":[subQ1,subQ0]});Q3=makeQuery(id+"F10.imprint","IMPRINT",FACE,{"disambiguationData":[TD([[makeQuery(id+"F10.imprint","IMPRINT",EDGE,{"disambiguationData":[TD([[subQ2,1.0]])],"derivedFrom":subQ1}),1.0]])]});}
            var Q4;
            {var subQ0=sQuery(id+"F10.wireOp",EDGE,"E10");var subQ1=sQuery(id+"F10.wireOp",EDGE,"E7");var subQ2=makeQuery(id+"F10.imprint","INTERSECT",VERTEX,{"derivedFrom":[subQ1,subQ0]});Q4=makeQuery(id+"F10.imprint","IMPRINT",FACE,{"disambiguationData":[TD([[makeQuery(id+"F10.imprint","IMPRINT",EDGE,{"disambiguationData":[TD([[subQ2,1.0]])],"derivedFrom":subQ1}),1.0]])]});}
            var Q5;
            {var subQ0=sQuery(id+"F10.wireOp",EDGE,"E10");var subQ1=sQuery(id+"F10.wireOp",EDGE,"E3");var subQ2=makeQuery(id+"F10.imprint","INTERSECT",VERTEX,{"derivedFrom":[subQ1,subQ0]});Q5=makeQuery(id+"F10.imprint","IMPRINT",FACE,{"disambiguationData":[TD([[makeQuery(id+"F10.imprint","IMPRINT",EDGE,{"disambiguationData":[TD([[subQ2,1.0]])],"derivedFrom":subQ1}),-1.0]])]});}
            var Q6;
            {var subQ0=sQuery(id+"F10.wireOp",EDGE,"E10");var subQ1=sQuery(id+"F10.wireOp",EDGE,"E2");var subQ2=makeQuery(id+"F10.imprint","INTERSECT",VERTEX,{"derivedFrom":[subQ1,subQ0]});Q6=makeQuery(id+"F10.imprint","IMPRINT",FACE,{"disambiguationData":[TD([[makeQuery(id+"F10.imprint","IMPRINT",EDGE,{"disambiguationData":[TD([[subQ2,1.0]])],"derivedFrom":subQ1}),-1.0]])]});}
            var Q7;
            {var subQ0=sQuery(id+"F10.wireOp",EDGE,"E10");var subQ1=sQuery(id+"F10.wireOp",EDGE,"E2");var subQ2=makeQuery(id+"F10.imprint","INTERSECT",VERTEX,{"derivedFrom":[subQ1,subQ0]});Q7=makeQuery(id+"F10.imprint","IMPRINT",FACE,{"disambiguationData":[TD([[makeQuery(id+"F10.imprint","IMPRINT",EDGE,{"disambiguationData":[TD([[subQ2,1.0]])],"derivedFrom":subQ1}),1.0]])]});}
            var Q8;
            {var subQ0=sQuery(id+"F10.wireOp",EDGE,"E10");var subQ1=sQuery(id+"F10.wireOp",EDGE,"E1");var subQ2=makeQuery(id+"F10.imprint","INTERSECT",VERTEX,{"derivedFrom":[subQ1,subQ0]});Q8=makeQuery(id+"F10.imprint","IMPRINT",FACE,{"disambiguationData":[TD([[makeQuery(id+"F10.imprint","IMPRINT",EDGE,{"disambiguationData":[TD([[subQ2,1.0]])],"derivedFrom":subQ1}),-1.0]])]});}
            var Q9;
            {var subQ0=sQuery(id+"F10.wireOp",EDGE,"E10");var subQ1=sQuery(id+"F10.wireOp",EDGE,"E1");var subQ2=makeQuery(id+"F10.imprint","INTERSECT",VERTEX,{"derivedFrom":[subQ1,subQ0]});Q9=makeQuery(id+"F10.imprint","IMPRINT",FACE,{"disambiguationData":[TD([[makeQuery(id+"F10.imprint","IMPRINT",EDGE,{"disambiguationData":[TD([[subQ2,1.0]])],"derivedFrom":subQ1}),1.0]])]});}
            var Q10;
            {var subQ0=sQuery(id+"F10.wireOp",EDGE,"E10");var subQ1=sQuery(id+"F10.wireOp",EDGE,"E9");var subQ2=makeQuery(id+"F10.imprint","INTERSECT",VERTEX,{"derivedFrom":[subQ1,subQ0]});Q10=makeQuery(id+"F10.imprint","IMPRINT",FACE,{"disambiguationData":[TD([[makeQuery(id+"F10.imprint","IMPRINT",EDGE,{"disambiguationData":[TD([[subQ2,1.0]])],"derivedFrom":subQ1}),1.0]])]});}
            var Q11;
            Q11=sQuery(id+"F10.wireOp",EDGE,"E10");
            revolve(context, id + "F32", {"entities" : qUnion([Q0, Q1, Q2, Q3, Q4, Q5, Q6, Q7, Q8, Q9, Q10]), "axis" : qUnion([Q11]), "revolveType" : RevolveType.FULL});
        }
        {
            var Q0;
            Q0=qCreatedBy(makeId("Top.planeOp"),FACE);
            var sketch = newSketch(context, id + "F33", { "sketchPlane" : qUnion([Q0])});
            skCircle(sketch, "E14", {"center": v(816.62, 0) * mm, "radius": 71.5 * mm, "construction": true});
            skLineSegment(sketch, "E15", {"start": v(816.62, 71.5) * mm, "end": v(1212.3, 71.5) * mm});
            skLineSegment(sketch, "E16", {"start": v(816.62, -71.5) * mm, "end": v(1212.3, -71.5) * mm});
            skLineSegment(sketch, "E17", {"start": v(816.62, -71.5) * mm, "end": v(655.7, -71.5) * mm});
            skLineSegment(sketch, "E18", {"start": v(655.7, -71.5) * mm, "end": v(655.7, 71.5) * mm});
            skLineSegment(sketch, "E19", {"start": v(655.7, 71.5) * mm, "end": v(816.62, 71.5) * mm});
            skLineSegment(sketch, "E20", {"start": v(1212.3, -71.5) * mm, "end": v(1212.3, 71.5) * mm});
            skSolve(sketch);
        }
        {
            var Q0;
            Q0=makeQuery(id+"F33.imprint","IMPRINT",FACE,{"disambiguationData":[TD([[makeQuery(id+"F33.imprint","IMPRINT",EDGE,{"derivedFrom":sQuery(id+"F33.wireOp",EDGE,"E15")}),-1.0]])]});
            var Q1;
            Q1=sQuery(id+"F33.wireOp",EDGE,"E14");
            var Q2;
            Q2=makeQuery(id+"F19.opRevolve","SWEPT_BODY",BODY,{"disambiguationData":[OSD([sQuery(id+"F10.wireOp",EDGE,"E5"),sQuery(id+"F10.wireOp",EDGE,"E10"),sQuery(id+"F10.wireOp",EDGE,"E11")])]});
            extrude(context, id + "F34", {"entities" : qUnion([Q0]), "surfaceEntities" : qUnion([Q1]), "endBoundEntityBody" : qUnion([Q2]), "depth" : 25 * mm});
        }
        {
            var Q0;
            Q0=makeQuery(id+"F34.opExtrude","CAP_FACE",FACE,{"disambiguationData":[OSD([sQuery(id+"F33.wireOp",EDGE,"E15"),sQuery(id+"F33.wireOp",EDGE,"E16"),sQuery(id+"F33.wireOp",EDGE,"E17"),sQuery(id+"F33.wireOp",EDGE,"E18"),sQuery(id+"F33.wireOp",EDGE,"E19"),sQuery(id+"F33.wireOp",EDGE,"E20")])],"isStart":true});
            extrude(context, id + "F35", {"entities" : qUnion([Q0]), "depth" : 251 * mm});
        }
        {
            var Q0;
            Q0=makeQuery(id+"F35.opExtrude","SWEPT_BODY",BODY,{"disambiguationData":[OSD([sQuery(id+"F33.wireOp",EDGE,"E15"),sQuery(id+"F33.wireOp",EDGE,"E16"),sQuery(id+"F33.wireOp",EDGE,"E17"),sQuery(id+"F33.wireOp",EDGE,"E18"),sQuery(id+"F33.wireOp",EDGE,"E19"),sQuery(id+"F33.wireOp",EDGE,"E20")])]});
            var Q1;
            Q1=makeQuery(id+"F32.opRevolve","SWEPT_BODY",BODY,{"disambiguationData":[OSD([sQuery(id+"F10.wireOp",EDGE,"E0"),sQuery(id+"F10.wireOp",EDGE,"E10"),sQuery(id+"F10.wireOp",EDGE,"E11")])]});
            booleanBodies(context, id + "F36", {"operationType" : BooleanOperationType.INTERSECTION, "tools" : qUnion([Q0, Q1]), "keepTools" : true});
        }
        {
            var Q0;
            Q0=makeQuery(id+"F34.opExtrude","CAP_FACE",FACE,{"disambiguationData":[OSD([sQuery(id+"F33.wireOp",EDGE,"E15"),sQuery(id+"F33.wireOp",EDGE,"E16"),sQuery(id+"F33.wireOp",EDGE,"E17"),sQuery(id+"F33.wireOp",EDGE,"E18"),sQuery(id+"F33.wireOp",EDGE,"E19"),sQuery(id+"F33.wireOp",EDGE,"E20")])],"isStart":false});
            var sketch = newSketch(context, id + "F37", { "sketchPlane" : qUnion([Q0])});
            skLineSegment(sketch, "E21.0.0", {"start": v(655.7, 71.5) * mm, "end": v(655.7, -71.5) * mm, "construction": true});
            skLineSegment(sketch, "E21.0.1", {"start": v(655.7, -71.5) * mm, "end": v(1212.3, -71.5) * mm, "construction": true});
            skLineSegment(sketch, "E21.0.2", {"start": v(1212.3, -71.5) * mm, "end": v(1212.3, 71.5) * mm, "construction": true});
            skLineSegment(sketch, "E21.0.3", {"start": v(1212.3, 71.5) * mm, "end": v(655.7, 71.5) * mm, "construction": true});
            skLineSegment(sketch, "E22.0", {"start": v(1278.54, 137.75) * mm, "end": v(589.46, 137.75) * mm});
            skLineSegment(sketch, "E22.1", {"start": v(1278.54, -137.75) * mm, "end": v(1278.54, 137.75) * mm});
            skLineSegment(sketch, "E22.2", {"start": v(589.46, -137.75) * mm, "end": v(1278.54, -137.75) * mm});
            skLineSegment(sketch, "E22.3", {"start": v(589.46, 137.75) * mm, "end": v(589.46, -137.75) * mm});
            skSolve(sketch);
        }
        {
            var Q0;
            Q0=makeQuery(id+"F37.imprint","IMPRINT",FACE,{"disambiguationData":[TD([[makeQuery(id+"F37.imprint","IMPRINT",EDGE,{"derivedFrom":sQuery(id+"F37.wireOp",EDGE,"E22.0")}),1.0]])]});
            var Q1;
            Q1=makeQuery(id+"F37.imprint","IMPRINT",FACE,{"disambiguationData":[TD([[makeQuery(id+"F37.imprint","IMPRINT",EDGE,{"derivedFrom":makeQuery(id+"F34.opExtrude","CAP_EDGE",EDGE,{"disambiguationData":[OSD([sQuery(id+"F33.wireOp",EDGE,"E18")])],"isStart":false})}),-1.0]])]});
            extrude(context, id + "F38", {"entities" : qUnion([Q0, Q1]), "operationType" : NewBodyOperationType.REMOVE, "depth" : 71 * mm});
        }
        {
            var Q0;
            Q0=makeQuery(id+"F34.opExtrude","SWEPT_BODY",BODY,{"disambiguationData":[OSD([sQuery(id+"F33.wireOp",EDGE,"E15"),sQuery(id+"F33.wireOp",EDGE,"E16"),sQuery(id+"F33.wireOp",EDGE,"E17"),sQuery(id+"F33.wireOp",EDGE,"E18"),sQuery(id+"F33.wireOp",EDGE,"E19"),sQuery(id+"F33.wireOp",EDGE,"E20")])]});
            var Q1;
            Q1=makeQuery(id+"F34.opExtrude","CAP_VERTEX",VERTEX,{"disambiguationData":[OSD([sQuery(id+"F33.wireOp",EDGE,"E18"),sQuery(id+"F33.wireOp",EDGE,"E19")])],"isStart":false});
            transform(context, id + "F39", {"entities" : qUnion([Q0]), "transformType" : TransformType.SCALE_UNIFORMLY, "scale" : 150 / 556, "scalePoint" : qUnion([Q1]), "makeCopy" : false});
        }
    });
